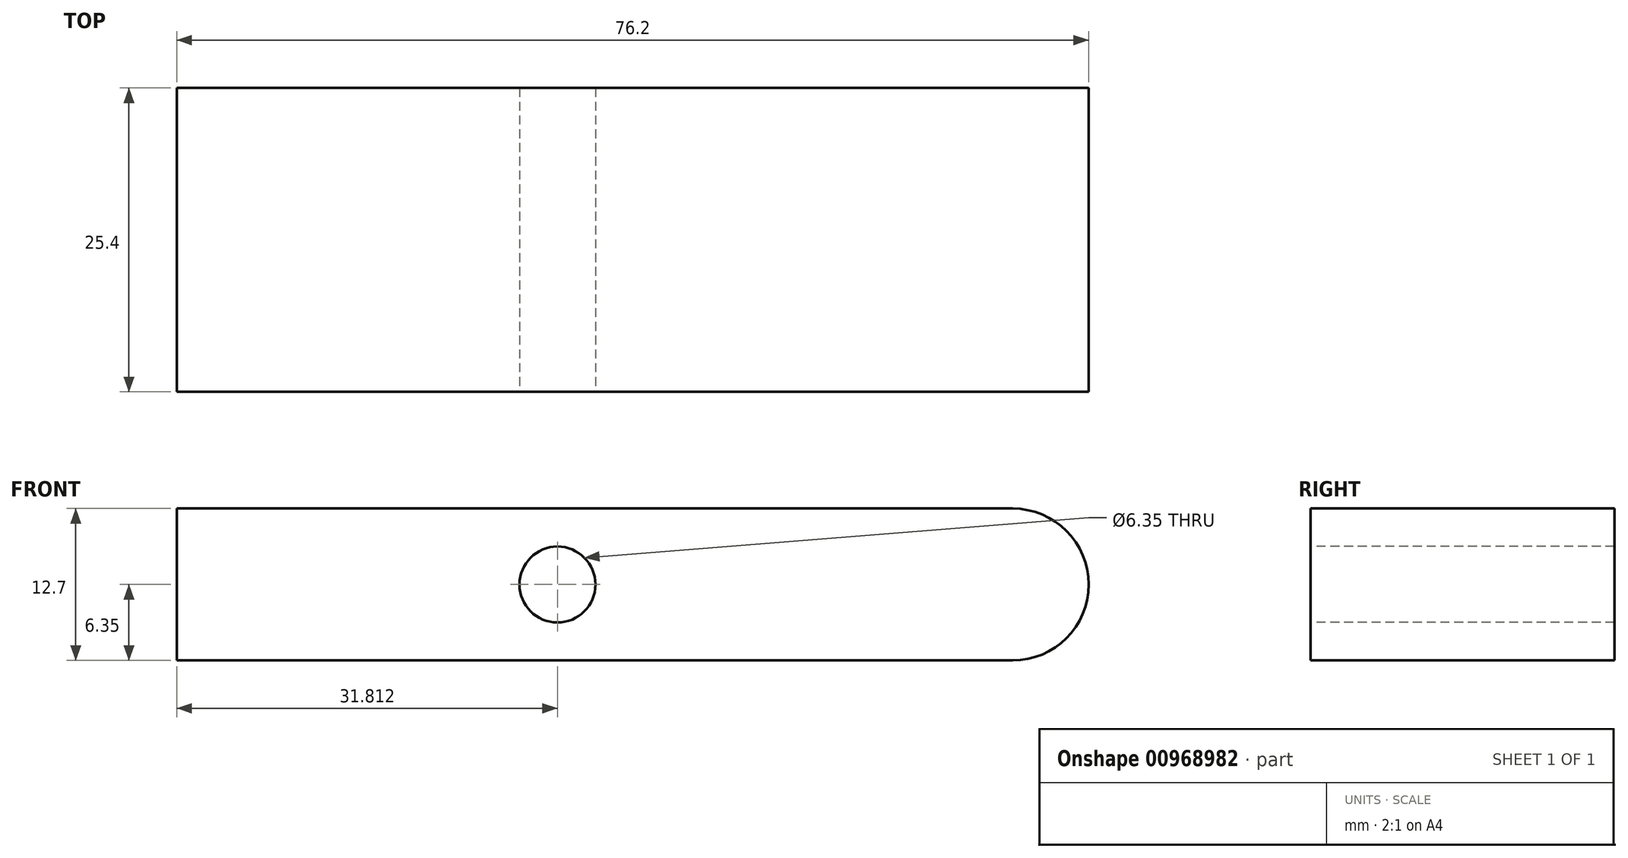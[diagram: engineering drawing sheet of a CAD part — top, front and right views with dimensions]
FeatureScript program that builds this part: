
annotation { "Feature Type Name" : "Feature", "Feature Type Description" : "" }
export const myFeature = defineFeature(function(context is Context, id is Id, definition is map)
    precondition{}
    {
        {
            var Q0;
            Q0=qCreatedBy(makeId("Front.planeOp"),FACE);
            var sketch = newSketch(context, id + "F0", { "sketchPlane" : qUnion([Q0])});
            skLineSegment(sketch, "E0.bottom", {"start": v(31.75, 6.35) * mm, "end": v(-38.1, 6.35) * mm});
            skLineSegment(sketch, "E0.top", {"start": v(31.75, -6.35) * mm, "end": v(-38.1, -6.35) * mm});
            skLineSegment(sketch, "E0.left", {"start": v(38.1, 0) * mm, "end": v(38.1, 0) * mm});
            skLineSegment(sketch, "E0.right", {"start": v(-38.1, 6.35) * mm, "end": v(-38.1, -6.35) * mm});
            skPoint(sketch, "E0.middle", {"position": v(0, 0) * mm});
            skPoint(sketch, "E1.visualSharp", {"position": v(38.1, 6.35) * mm});
            skArc(sketch, "E1.filletArc", {"start": v(38.1, 0) * mm, "mid": v(36.24, 4.5) * mm, "end": v(31.75, 6.35) * mm});
            skPoint(sketch, "E2.visualSharp", {"position": v(38.1, -6.35) * mm});
            skArc(sketch, "E2.filletArc", {"start": v(31.75, -6.35) * mm, "mid": v(36.24, -4.5) * mm, "end": v(38.1, 0) * mm});
            skSolve(sketch);
        }
        {
            var Q0;
            Q0 = qSketchRegion(id + "F0", true);
            extrude(context, id + "F1", {"entities" : qUnion([Q0]), "depth" : 25.4 * mm, "offsetDistance" : 25.4 * mm});
        }
        {
            var Q0;
            Q0=makeQuery(id+"F1.opExtrude","CAP_FACE",FACE,{"disambiguationData":[OSD([sQuery(id+"F0.wireOp",EDGE,"E0.bottom"),sQuery(id+"F0.wireOp",EDGE,"E0.top"),sQuery(id+"F0.wireOp",EDGE,"E0.right"),sQuery(id+"F0.wireOp",EDGE,"E1.filletArc"),sQuery(id+"F0.wireOp",EDGE,"E2.filletArc")])],"isStart":false});
            var sketch = newSketch(context, id + "F2", { "sketchPlane" : qUnion([Q0])});
            skCircle(sketch, "E3", {"center": v(-6.29, 0) * mm, "radius": 3.18 * mm});
            skLineSegment(sketch, "E4", {"start": v(-6.29, 0) * mm, "end": v(38.1, 0) * mm});
            skSolve(sketch);
        }
        {
            var Q0;
            Q0=makeQuery(id+"F2.imprint","IMPRINT",FACE,{"disambiguationData":[TD([[makeQuery(id+"F2.imprint","IMPRINT",EDGE,{"derivedFrom":sQuery(id+"F2.wireOp",EDGE,"E3")}),1.0]])]});
            extrude(context, id + "F3", {"entities" : qUnion([Q0]), "operationType" : NewBodyOperationType.REMOVE, "oppositeDirection" : true, "depth" : 25.4 * mm, "offsetDistance" : 25.4 * mm});
        }
    });
